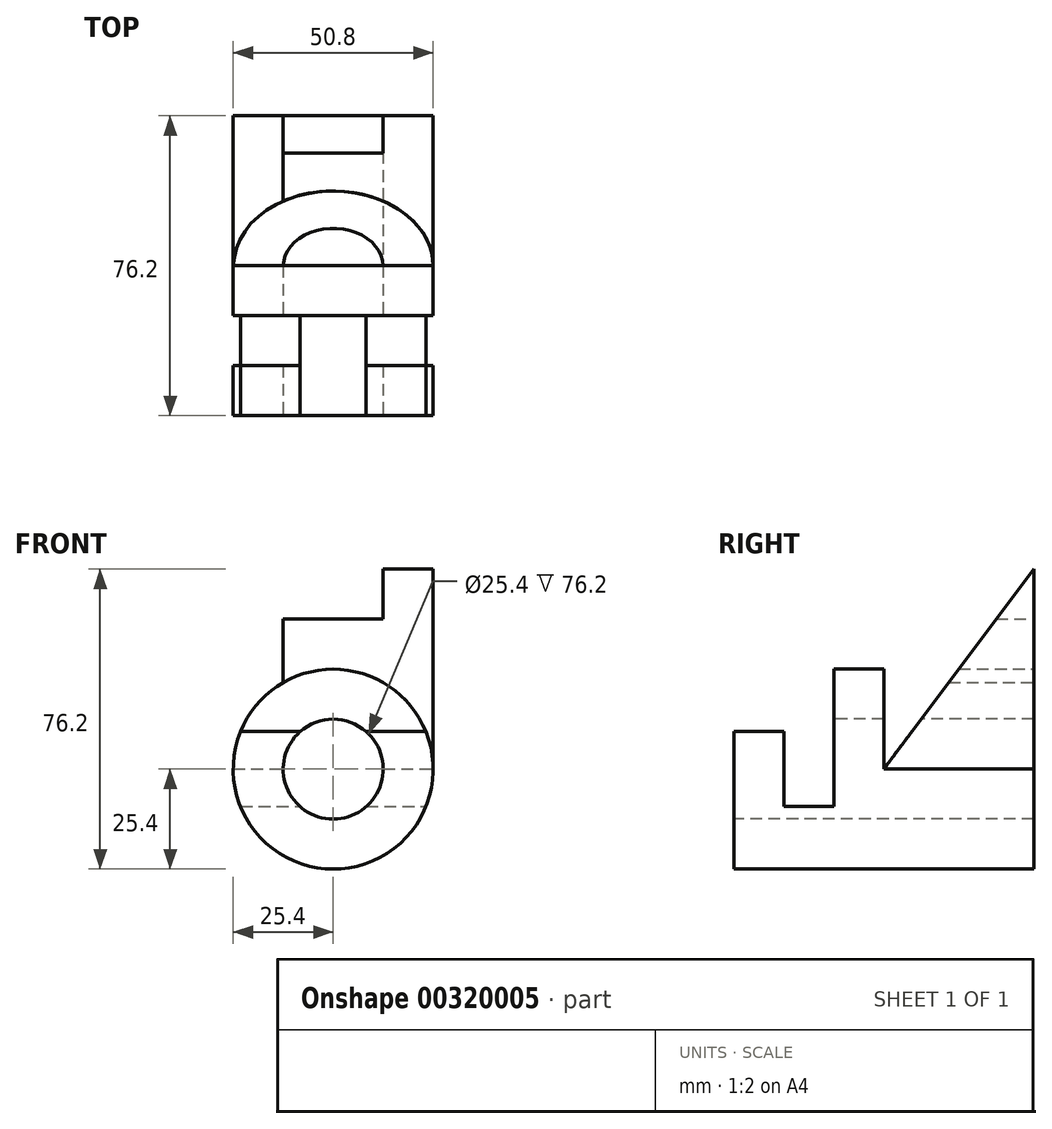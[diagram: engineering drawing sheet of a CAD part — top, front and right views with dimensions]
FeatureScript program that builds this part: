
annotation { "Feature Type Name" : "Feature", "Feature Type Description" : "" }
export const myFeature = defineFeature(function(context is Context, id is Id, definition is map)
    precondition{}
    {
        {
            var Q0;
            Q0=qCreatedBy(makeId("Front.planeOp"),FACE);
            var sketch = newSketch(context, id + "F0", { "sketchPlane" : qUnion([Q0])});
            skCircle(sketch, "E0", {"center": v(0, 0) * mm, "radius": 25.4 * mm});
            skLineSegment(sketch, "E1", {"start": v(-12.7, 22) * mm, "end": v(-12.7, 38.1) * mm});
            skLineSegment(sketch, "E2", {"start": v(-12.7, 38.1) * mm, "end": v(12.7, 38.1) * mm});
            skLineSegment(sketch, "E3", {"start": v(12.7, 38.1) * mm, "end": v(12.7, 50.8) * mm});
            skLineSegment(sketch, "E4", {"start": v(12.7, 50.8) * mm, "end": v(25.4, 50.8) * mm});
            skLineSegment(sketch, "E5", {"start": v(25.4, 50.8) * mm, "end": v(25.4, 0) * mm});
            skLineSegment(sketch, "E6", {"start": v(0, 0) * mm, "end": v(0, 38.1) * mm, "construction": true});
            skSolve(sketch);
        }
        {
            var Q0;
            {var subQ0=sQuery(id+"F0.wireOp",EDGE,"E0");var subQ1=makeQuery(id+"F0.imprint","INTERSECT",VERTEX,{"derivedFrom":[subQ0,sQuery(id+"F0.wireOp",EDGE,"E1")]});Q0=makeQuery(id+"F0.imprint","IMPRINT",FACE,{"disambiguationData":[TD([[makeQuery(id+"F0.imprint","IMPRINT",EDGE,{"disambiguationData":[TD([[subQ1,1.0]])],"derivedFrom":subQ0}),1.0]])]});}
            extrude(context, id + "F1", {"entities" : qUnion([Q0]), "depth" : 76.2 * mm});
        }
        {
            var Q0;
            {var subQ0=sQuery(id+"F0.wireOp",EDGE,"E1");Q0=makeQuery(id+"F0.imprint","IMPRINT",FACE,{"disambiguationData":[TD([[makeQuery(id+"F0.imprint","IMPRINT",EDGE,{"derivedFrom":subQ0}),-1.0]])]});}
            extrude(context, id + "F2", {"entities" : qUnion([Q0]), "depth" : 38.1 * mm});
        }
        {
            var Q0;
            Q0=makeQuery(id+"F2.opExtrude","SWEPT_FACE",FACE,{"disambiguationData":[OSD([sQuery(id+"F0.wireOp",EDGE,"E5")])]});
            var sketch = newSketch(context, id + "F3", { "sketchPlane" : qUnion([Q0])});
            skLineSegment(sketch, "E7", {"start": v(-38.1, 0) * mm, "end": v(0, 50.8) * mm});
            skLineSegment(sketch, "E8", {"start": v(0, 50.8) * mm, "end": v(-38.1, 50.8) * mm});
            skLineSegment(sketch, "E9", {"start": v(-38.1, 50.8) * mm, "end": v(-38.1, 0) * mm});
            skSolve(sketch);
        }
        {
            var Q0;
            Q0=makeQuery(id+"F3.imprint","IMPRINT",FACE,{"disambiguationData":[TD([[makeQuery(id+"F3.imprint","IMPRINT",EDGE,{"derivedFrom":sQuery(id+"F3.wireOp",EDGE,"E7")}),1.0]])]});
            extrude(context, id + "F4", {"entities" : qUnion([Q0]), "operationType" : NewBodyOperationType.REMOVE, "endBound" : BoundingType.THROUGH_ALL, "oppositeDirection" : true, "depth" : 25.4 * mm});
        }
        {
            var Q0;
            Q0=makeQuery(id+"F1.opExtrude","CAP_FACE",FACE,{"disambiguationData":[OSD([sQuery(id+"F0.wireOp",EDGE,"E0")])],"isStart":false});
            var sketch = newSketch(context, id + "F5", { "sketchPlane" : qUnion([Q0])});
            skCircle(sketch, "E10", {"center": v(0, 0) * mm, "radius": 12.7 * mm});
            skSolve(sketch);
        }
        {
            var Q0;
            Q0 = qSketchRegion(id + "F5", true);
            extrude(context, id + "F6", {"entities" : qUnion([Q0]), "operationType" : NewBodyOperationType.REMOVE, "endBound" : BoundingType.THROUGH_ALL, "oppositeDirection" : true, "depth" : 25.4 * mm});
        }
        {
            var Q0;
            Q0=makeQuery(id+"F1.opExtrude","CAP_FACE",FACE,{"disambiguationData":[OSD([sQuery(id+"F0.wireOp",EDGE,"E0")])],"isStart":false});
            var sketch = newSketch(context, id + "F7", { "sketchPlane" : qUnion([Q0])});
            skLineSegment(sketch, "E11", {"start": v(0, 25.4) * mm, "end": v(0, 9.53) * mm});
            skLineSegment(sketch, "E12", {"start": v(-23.55, 9.53) * mm, "end": v(23.55, 9.53) * mm});
            skArc(sketch, "E13.0", {"start": v(23.55, 9.53) * mm, "mid": v(0, 25.4) * mm, "end": v(-23.55, 9.53) * mm});
            skSolve(sketch);
        }
        {
            var Q0;
            Q0 = qSketchRegion(id + "F7", true);
            extrude(context, id + "F8", {"entities" : qUnion([Q0]), "operationType" : NewBodyOperationType.REMOVE, "oppositeDirection" : true, "depth" : 25.4 * mm});
        }
        {
            var Q0;
            Q0=qCreatedBy(makeId("Right.planeOp"),FACE);
            var sketch = newSketch(context, id + "F9", { "sketchPlane" : qUnion([Q0])});
            skLineSegment(sketch, "E14.bottom", {"start": v(-50.8, 25.4) * mm, "end": v(-63.5, 25.4) * mm});
            skLineSegment(sketch, "E14.top", {"start": v(-50.8, -9.53) * mm, "end": v(-63.5, -9.53) * mm});
            skLineSegment(sketch, "E14.left", {"start": v(-50.8, 25.4) * mm, "end": v(-50.8, -9.53) * mm});
            skLineSegment(sketch, "E14.right", {"start": v(-63.5, 25.4) * mm, "end": v(-63.5, -9.53) * mm});
            skLineSegment(sketch, "E15.0", {"start": v(-50.8, 9.53) * mm, "end": v(-50.8, 25.4) * mm});
            skSolve(sketch);
        }
        {
            var Q0;
            Q0 = qSketchRegion(id + "F9", true);
            extrude(context, id + "F10", {"entities" : qUnion([Q0]), "operationType" : NewBodyOperationType.REMOVE, "endBound" : BoundingType.THROUGH_ALL, "oppositeDirection" : true, "depth" : 25.4 * mm, "hasSecondDirection" : true, "secondDirectionBound" : SecondDirectionBoundingType.THROUGH_ALL, "secondDirectionOppositeDirection" : false, "secondDirectionDepth" : 25.4 * mm});
        }
    });
